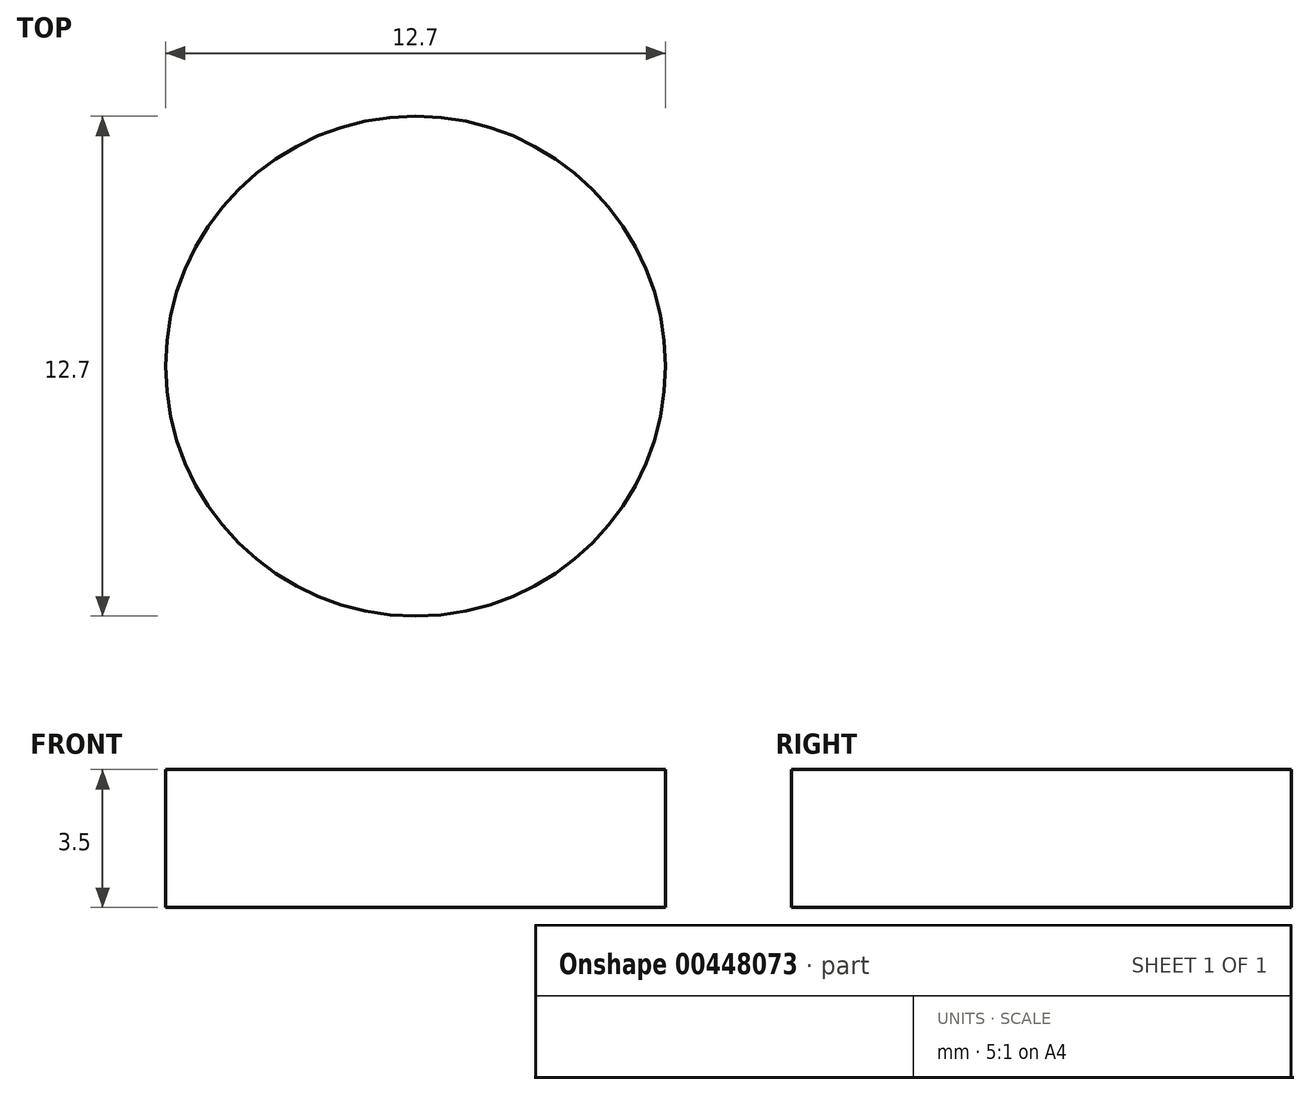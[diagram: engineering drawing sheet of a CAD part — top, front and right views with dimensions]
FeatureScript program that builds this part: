
annotation { "Feature Type Name" : "Feature", "Feature Type Description" : "" }
export const myFeature = defineFeature(function(context is Context, id is Id, definition is map)
    precondition{}
    {
        {
            assignVariable(context, id + "F0", {"name" : "ShaftL", "anyValue" : 3.5});
        }
        {
            var Q0;
            Q0=qCreatedBy(makeId("Top.planeOp"),FACE);
            var sketch = newSketch(context, id + "F1", { "sketchPlane" : qUnion([Q0])});
            skCircle(sketch, "E0.cCircle", {"center": v(0, 0) * mm, "radius": 6.35 * mm, "construction": true});
            skPoint(sketch, "E0.0.midPoint", {"position": v(0, 6.35) * mm});
            skCircle(sketch, "E1", {"center": v(0, 0) * mm, "radius": 6.35 * mm});
            skSolve(sketch);
        }
        {
            var Q0;
            Q0=makeQuery(id+"F1.imprint","IMPRINT",FACE,{"disambiguationData":[TD([[makeQuery(id+"F1.imprint","IMPRINT",EDGE,{"derivedFrom":sQuery(id+"F1.wireOp",EDGE,"E1")}),1.0]])]});
            extrude(context, id + "F2", {"entities" : qUnion([Q0]), "depth" : (getVariable(context, 'ShaftL')) * mm});
        }
    });
